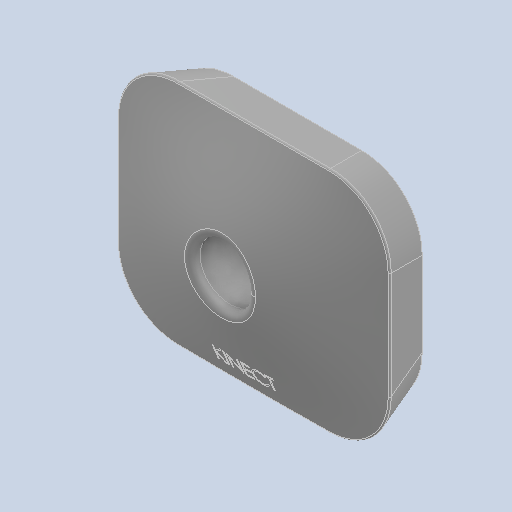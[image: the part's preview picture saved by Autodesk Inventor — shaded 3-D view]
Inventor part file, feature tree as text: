
AUTODESK INVENTOR PART (.ipt)
format: ipt  version: 2024 (Build 280153000, 153)  size: 369,664 bytes
history: native  units: in
note: dims shown in document units (in); Inventor stores cm internally (conversion verified against a paired STEP export)
features: other x1, fillet x1
ambient origin geometry x8: Origin, YZ Plane, XZ Plane, XY Plane, X Axis, Y Axis, Z Axis, Center Point
bodies: Solid1 (feature_tree)
feature tree (2):
  other  "Plane1"
  fillet  "Fillet3"  [1 undecoded]
note: 1 required parameter value undecoded (feature->parameter linkage not recoverable at this tier; creation-order binding heuristic only, values carry confidence <= 0.55)
